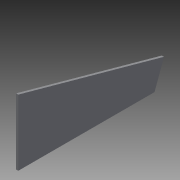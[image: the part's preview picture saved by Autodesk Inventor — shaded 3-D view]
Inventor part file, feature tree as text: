
AUTODESK INVENTOR PART (.ipt)
format: ipt  version: 2014 SP2 (Build 180246200, 246)  size: 70,656 bytes
history: native  units: mm
features: extrude x1, sketch x1
ambient origin geometry x8: Origin, YZ Plane, XZ Plane, XY Plane, X Axis, Y Axis, Z Axis, Center Point
bodies: Solid1 (feature_tree)
feature tree (2):
  extrude  "Extrusion1"  TaperAngle=90.0deg  [1 undecoded]
  sketch  "Sketch1"  dims[d4=4.0mm d5=0.0mm d7=90.0deg d8=243.0mm d9=18.675023mm d10=49.0mm d11=115.0mm]
note: 1 required parameter value undecoded (feature->parameter linkage not recoverable at this tier; creation-order binding heuristic only, values carry confidence <= 0.55)
